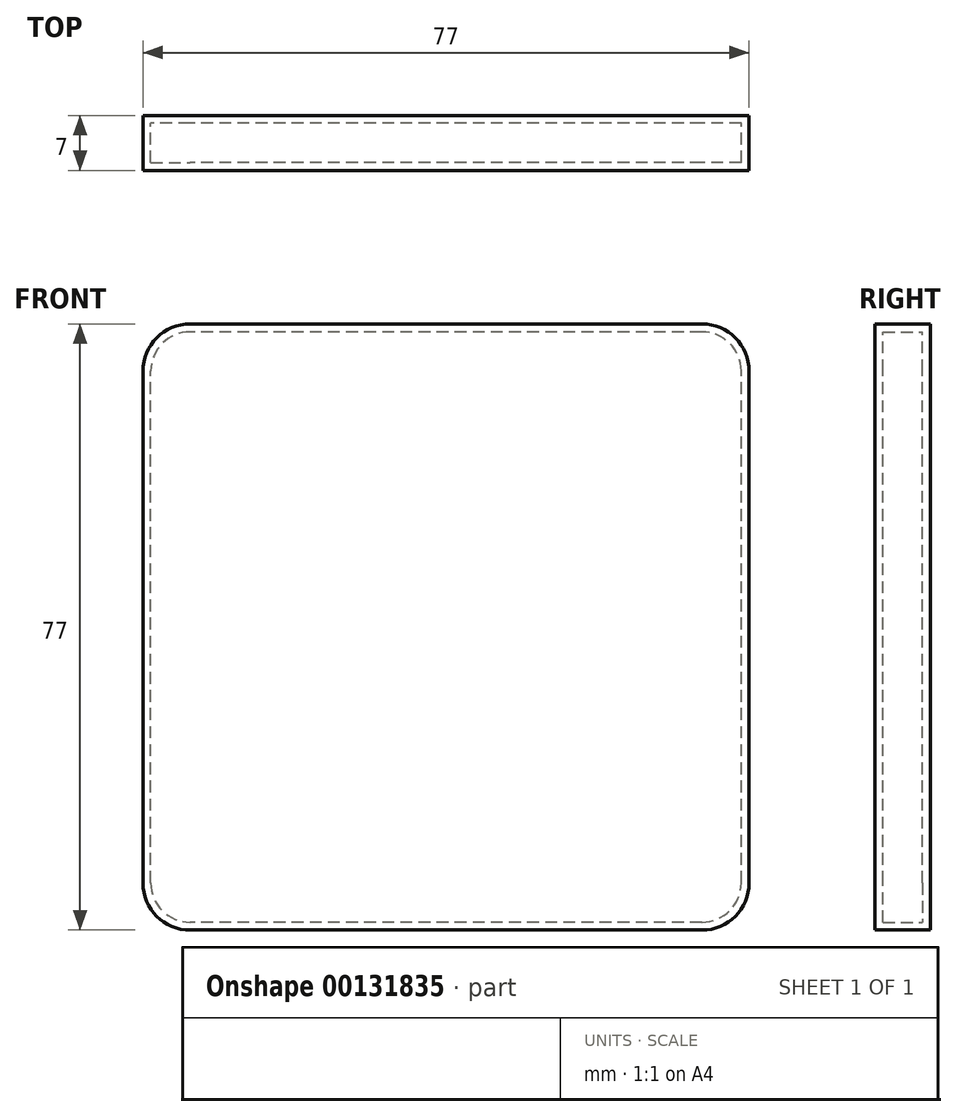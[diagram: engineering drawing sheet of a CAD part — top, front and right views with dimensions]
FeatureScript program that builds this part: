
annotation { "Feature Type Name" : "Feature", "Feature Type Description" : "" }
export const myFeature = defineFeature(function(context is Context, id is Id, definition is map)
    precondition{}
    {
        {
            var Q0;
            Q0=qCreatedBy(makeId("Front.planeOp"),FACE);
            var sketch = newSketch(context, id + "F0", { "sketchPlane" : qUnion([Q0])});
            skLineSegment(sketch, "E0.bottom", {"start": v(32.5, -37.5) * mm, "end": v(-32.5, -37.5) * mm});
            skLineSegment(sketch, "E0.top", {"start": v(32.5, 37.5) * mm, "end": v(-32.5, 37.5) * mm});
            skLineSegment(sketch, "E0.left", {"start": v(37.5, -32.5) * mm, "end": v(37.5, 32.5) * mm});
            skLineSegment(sketch, "E0.right", {"start": v(-37.5, -32.5) * mm, "end": v(-37.5, 32.5) * mm});
            skPoint(sketch, "E0.middle", {"position": v(0, 0) * mm});
            skLineSegment(sketch, "E1.bottom", {"start": v(32.5, -38.5) * mm, "end": v(-32.5, -38.5) * mm});
            skLineSegment(sketch, "E1.top", {"start": v(32.5, 38.5) * mm, "end": v(-32.5, 38.5) * mm});
            skLineSegment(sketch, "E1.left", {"start": v(38.5, -32.5) * mm, "end": v(38.5, 32.5) * mm});
            skLineSegment(sketch, "E1.right", {"start": v(-38.5, -32.5) * mm, "end": v(-38.5, 32.5) * mm});
            skArc(sketch, "E2", {"start": v(-32.5, 37.5) * mm, "mid": v(-36.04, 36.04) * mm, "end": v(-37.5, 32.5) * mm});
            skArc(sketch, "E3", {"start": v(-32.5, 38.5) * mm, "mid": v(-36.74, 36.74) * mm, "end": v(-38.5, 32.5) * mm});
            skArc(sketch, "E4", {"start": v(37.5, 32.5) * mm, "mid": v(36.04, 36.04) * mm, "end": v(32.5, 37.5) * mm});
            skArc(sketch, "E5", {"start": v(38.5, 32.5) * mm, "mid": v(36.74, 36.74) * mm, "end": v(32.5, 38.5) * mm});
            skArc(sketch, "E6", {"start": v(32.5, -37.5) * mm, "mid": v(36.04, -36.04) * mm, "end": v(37.5, -32.5) * mm});
            skArc(sketch, "E7", {"start": v(32.5, -38.5) * mm, "mid": v(36.74, -36.74) * mm, "end": v(38.5, -32.5) * mm});
            skArc(sketch, "E8", {"start": v(-37.5, -32.5) * mm, "mid": v(-36.04, -36.04) * mm, "end": v(-32.5, -37.5) * mm});
            skArc(sketch, "E9", {"start": v(-38.5, -32.5) * mm, "mid": v(-36.74, -36.74) * mm, "end": v(-32.5, -38.5) * mm});
            skSolve(sketch);
        }
        {
            var Q0;
            Q0=makeQuery(id+"F0.imprint","IMPRINT",FACE,{"disambiguationData":[TD([[makeQuery(id+"F0.imprint","IMPRINT",EDGE,{"derivedFrom":sQuery(id+"F0.wireOp",EDGE,"E0.bottom")}),1.0]])]});
            extrude(context, id + "F1", {"entities" : qUnion([Q0]), "depth" : 5 * mm});
        }
        {
            var Q0;
            Q0=makeQuery(id+"F1.opExtrude","CAP_FACE",FACE,{"disambiguationData":[OSD([sQuery(id+"F0.wireOp",EDGE,"E0.bottom"),sQuery(id+"F0.wireOp",EDGE,"E0.top"),sQuery(id+"F0.wireOp",EDGE,"E0.left"),sQuery(id+"F0.wireOp",EDGE,"E0.right"),sQuery(id+"F0.wireOp",EDGE,"E1.bottom"),sQuery(id+"F0.wireOp",EDGE,"E1.top"),sQuery(id+"F0.wireOp",EDGE,"E1.left"),sQuery(id+"F0.wireOp",EDGE,"E1.right"),sQuery(id+"F0.wireOp",EDGE,"E2"),sQuery(id+"F0.wireOp",EDGE,"E3"),sQuery(id+"F0.wireOp",EDGE,"E4"),sQuery(id+"F0.wireOp",EDGE,"E5"),sQuery(id+"F0.wireOp",EDGE,"E6"),sQuery(id+"F0.wireOp",EDGE,"E7"),sQuery(id+"F0.wireOp",EDGE,"E8"),sQuery(id+"F0.wireOp",EDGE,"E9")])],"isStart":false});
            var sketch = newSketch(context, id + "F2", { "sketchPlane" : qUnion([Q0])});
            skSolve(sketch);
        }
        {
            var Q0;
            Q0=makeQuery(id+"F2.imprint","IMPRINT",FACE,{"disambiguationData":[TD([[makeQuery(id+"F2.imprint","IMPRINT",EDGE,{"derivedFrom":makeQuery(id+"F1.opExtrude","CAP_EDGE",EDGE,{"disambiguationData":[OSD([sQuery(id+"F0.wireOp",EDGE,"E0.bottom")])],"isStart":false})}),1.0]])]});
            var Q1;
            Q1 = qSketchRegion(id + "F2", true);
            var Q2;
            Q2=makeQuery(id+"F2.imprint","IMPRINT",FACE,{"disambiguationData":[TD([[makeQuery(id+"F2.imprint","IMPRINT",EDGE,{"derivedFrom":makeQuery(id+"F1.opExtrude","CAP_EDGE",EDGE,{"disambiguationData":[OSD([sQuery(id+"F0.wireOp",EDGE,"E0.bottom")])],"isStart":false})}),-1.0]])]});
            extrude(context, id + "F3", {"entities" : qUnion([Q0, Q1, Q2]), "operationType" : NewBodyOperationType.ADD, "depth" : 1 * mm});
        }
        {
            var Q0;
            Q0=makeQuery(id+"F1.opExtrude","CAP_FACE",FACE,{"disambiguationData":[OSD([sQuery(id+"F0.wireOp",EDGE,"E0.bottom"),sQuery(id+"F0.wireOp",EDGE,"E0.top"),sQuery(id+"F0.wireOp",EDGE,"E0.left"),sQuery(id+"F0.wireOp",EDGE,"E0.right"),sQuery(id+"F0.wireOp",EDGE,"E1.bottom"),sQuery(id+"F0.wireOp",EDGE,"E1.top"),sQuery(id+"F0.wireOp",EDGE,"E1.left"),sQuery(id+"F0.wireOp",EDGE,"E1.right"),sQuery(id+"F0.wireOp",EDGE,"E2"),sQuery(id+"F0.wireOp",EDGE,"E3"),sQuery(id+"F0.wireOp",EDGE,"E4"),sQuery(id+"F0.wireOp",EDGE,"E5"),sQuery(id+"F0.wireOp",EDGE,"E6"),sQuery(id+"F0.wireOp",EDGE,"E7"),sQuery(id+"F0.wireOp",EDGE,"E8"),sQuery(id+"F0.wireOp",EDGE,"E9")])],"isStart":true});
            var sketch = newSketch(context, id + "F4", { "sketchPlane" : qUnion([Q0])});
            skSolve(sketch);
        }
        {
            var Q0;
            Q0=makeQuery(id+"F4.imprint","IMPRINT",FACE,{"disambiguationData":[TD([[makeQuery(id+"F4.imprint","IMPRINT",EDGE,{"derivedFrom":makeQuery(id+"F1.opExtrude","CAP_EDGE",EDGE,{"disambiguationData":[OSD([sQuery(id+"F0.wireOp",EDGE,"E0.bottom")])],"isStart":true})}),-1.0]])]});
            var Q1;
            Q1=makeQuery(id+"F4.imprint","IMPRINT",FACE,{"disambiguationData":[TD([[makeQuery(id+"F4.imprint","IMPRINT",EDGE,{"derivedFrom":makeQuery(id+"F1.opExtrude","CAP_EDGE",EDGE,{"disambiguationData":[OSD([sQuery(id+"F0.wireOp",EDGE,"E0.bottom")])],"isStart":true})}),1.0]])]});
            extrude(context, id + "F5", {"entities" : qUnion([Q0, Q1]), "operationType" : NewBodyOperationType.ADD, "depth" : 1 * mm});
        }
    });
